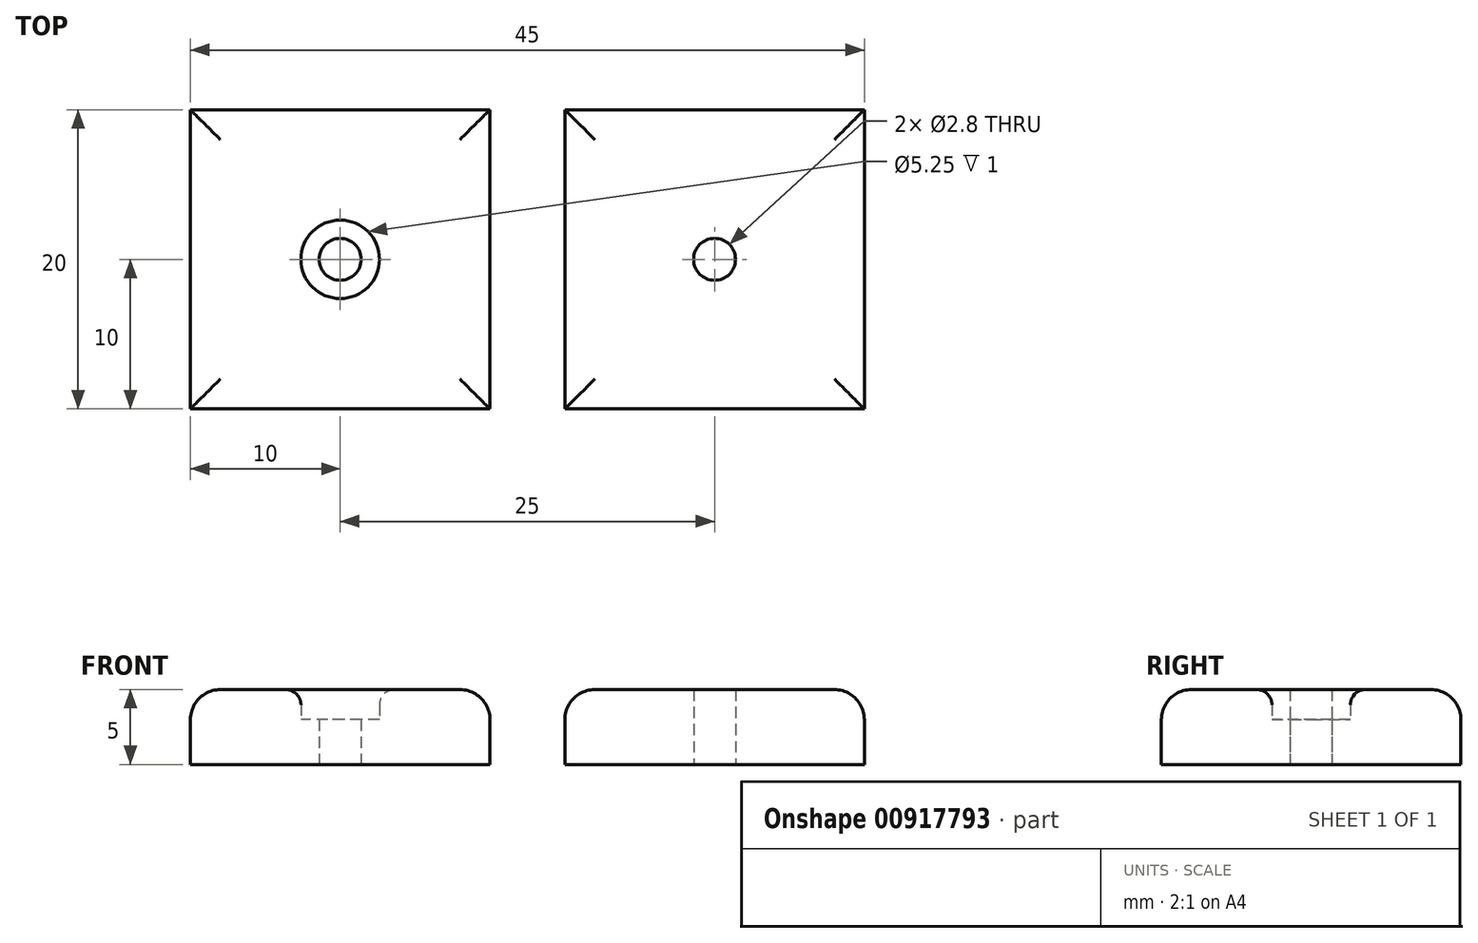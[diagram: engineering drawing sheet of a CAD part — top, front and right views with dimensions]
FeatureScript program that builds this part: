
annotation { "Feature Type Name" : "Feature", "Feature Type Description" : "" }
export const myFeature = defineFeature(function(context is Context, id is Id, definition is map)
    precondition{}
    {
        {
            var Q0;
            Q0=qCreatedBy(makeId("Top.planeOp"),FACE);
            var sketch = newSketch(context, id + "F0", { "sketchPlane" : qUnion([Q0])});
            skLineSegment(sketch, "E0.bottom", {"start": v(-10, 10) * mm, "end": v(10, 10) * mm});
            skLineSegment(sketch, "E0.top", {"start": v(-10, -10) * mm, "end": v(10, -10) * mm});
            skLineSegment(sketch, "E0.left", {"start": v(-10, 10) * mm, "end": v(-10, -10) * mm});
            skLineSegment(sketch, "E0.right", {"start": v(10, 10) * mm, "end": v(10, -10) * mm});
            skCircle(sketch, "E1", {"center": v(0, 0) * mm, "radius": 1.4 * mm});
            skCircle(sketch, "E2", {"center": v(0, 0) * mm, "radius": 2.62 * mm});
            skLineSegment(sketch, "E3.bottom", {"start": v(15, 10) * mm, "end": v(35, 10) * mm});
            skLineSegment(sketch, "E3.top", {"start": v(15, -10) * mm, "end": v(35, -10) * mm});
            skLineSegment(sketch, "E3.left", {"start": v(15, 10) * mm, "end": v(15, -10) * mm});
            skLineSegment(sketch, "E3.right", {"start": v(35, 10) * mm, "end": v(35, -10) * mm});
            skLineSegment(sketch, "E4", {"start": v(25, 10) * mm, "end": v(25, -10) * mm, "construction": true});
            skPoint(sketch, "E5", {"position": v(25, 0) * mm});
            skCircle(sketch, "E6", {"center": v(25, 0) * mm, "radius": 1.4 * mm});
            skSolve(sketch);
        }
        {
            var Q0;
            Q0 = qSketchRegion(id + "F0", true);
            extrude(context, id + "F1", {"entities" : qUnion([Q0]), "depth" : 5 * mm, "offsetDistance" : 25 * mm});
        }
        {
            var Q0;
            Q0=makeQuery(id+"F0.imprint","IMPRINT",FACE,{"disambiguationData":[TD([[makeQuery(id+"F0.imprint","IMPRINT",EDGE,{"derivedFrom":sQuery(id+"F0.wireOp",EDGE,"E1")}),-1.0]])]});
            extrude(context, id + "F2", {"entities" : qUnion([Q0]), "operationType" : NewBodyOperationType.ADD, "depth" : 3 * mm, "offsetDistance" : 25 * mm});
        }
        {
            var Q0;
            Q0=makeQuery(id+"F1.opExtrude","CAP_EDGE",EDGE,{"disambiguationData":[OSD([sQuery(id+"F0.wireOp",EDGE,"E0.right")])],"isStart":false});
            var Q1;
            Q1=makeQuery(id+"F1.opExtrude","CAP_EDGE",EDGE,{"disambiguationData":[OSD([sQuery(id+"F0.wireOp",EDGE,"E0.top")])],"isStart":false});
            var Q2;
            Q2=makeQuery(id+"F1.opExtrude","CAP_EDGE",EDGE,{"disambiguationData":[OSD([sQuery(id+"F0.wireOp",EDGE,"E0.bottom")])],"isStart":false});
            var Q3;
            Q3=makeQuery(id+"F1.opExtrude","CAP_EDGE",EDGE,{"disambiguationData":[OSD([sQuery(id+"F0.wireOp",EDGE,"E0.left")])],"isStart":false});
            var Q4;
            Q4=makeQuery(id+"F1.opExtrude","CAP_EDGE",EDGE,{"disambiguationData":[OSD([sQuery(id+"F0.wireOp",EDGE,"E3.top")])],"isStart":false});
            var Q5;
            Q5=makeQuery(id+"F1.opExtrude","CAP_EDGE",EDGE,{"disambiguationData":[OSD([sQuery(id+"F0.wireOp",EDGE,"E3.left")])],"isStart":false});
            var Q6;
            Q6=makeQuery(id+"F1.opExtrude","CAP_EDGE",EDGE,{"disambiguationData":[OSD([sQuery(id+"F0.wireOp",EDGE,"E3.bottom")])],"isStart":false});
            var Q7;
            Q7=makeQuery(id+"F1.opExtrude","CAP_EDGE",EDGE,{"disambiguationData":[OSD([sQuery(id+"F0.wireOp",EDGE,"E3.right")])],"isStart":false});
            fillet(context, id + "F3", {"entities" : qUnion([Q0, Q1, Q2, Q3, Q4, Q5, Q6, Q7]), "radius" : 2 * mm, "tangentPropagation" : true, "allowEdgeOverflow" : false});
        }
        {
            var Q0;
            Q0=makeQuery(id+"F1.opExtrude","CAP_EDGE",EDGE,{"disambiguationData":[OSD([sQuery(id+"F0.wireOp",EDGE,"E2")])],"isStart":false});
            fillet(context, id + "F4", {"entities" : qUnion([Q0]), "radius" : 1 * mm, "tangentPropagation" : true, "allowEdgeOverflow" : false});
        }
    });
